# Revit family: Halter C-Profil 35 längs, V4A
name_source: partatom
category: HLS-Bauteile
revit_build: Autodesk Revit 2017 (Build: 20190507_1515(x64)
units: mm (PartAtom-declared; Revit-internal decimal feet)

## family parameters
Basisbauteil = Fläche
Beim Laden mit Abzugskörper schneiden = Nein
Bemaßung runder Anschluss = Durchmesser verwenden
Gemeinsam genutzt = Ja
Raumberechnungspunkt = Nein
Teiletyp = Normal

## types (1)
- Halter C-Profil 35 längs, V4A
    Artikelnummer = 9993300
    Ausrichtung Platte = längs
    Befestigung = Baukörper
    Breite Platte = 45 mm  [stored 0.147638 ft]
    EAN = 4250928450333
    Fabrikat = MEFA
    Firma = MEFA Befestigungs- und Montagesysteme GmbH
    Gewicht = 0.24 kg
    Gewicht pro Bauteil = 0.24 kg
    Kurztext1 = Halter C-Profil 35 längs V4A
    Kurztext2 = für C-Profil 35
    Langloch = 11x15 mm
    Lochabstand = 70 mm
    Länge = 0 mm  [stored 0 ft]
    Länge Platte = 100 mm  [stored 0.328084 ft]
    Material = Edelstahl
    Profil = C-Profil
    Profilname = C-Profil 35
    Profiltyp = 35
    Sicherheitsfaktor = 0
    Stärke Platte = 4 mm  [stored 0.0131234 ft]
    Vorgabe-Ansicht = 1219 mm
    max. Profilhöhe = 21 mm  [stored 0.0688976 ft]
    max. zul. Last Druck = 0.00 kip

note: [stored X ft] marks values corroborated as IEEE doubles in the binary element streams (Revit-internal decimal feet)
